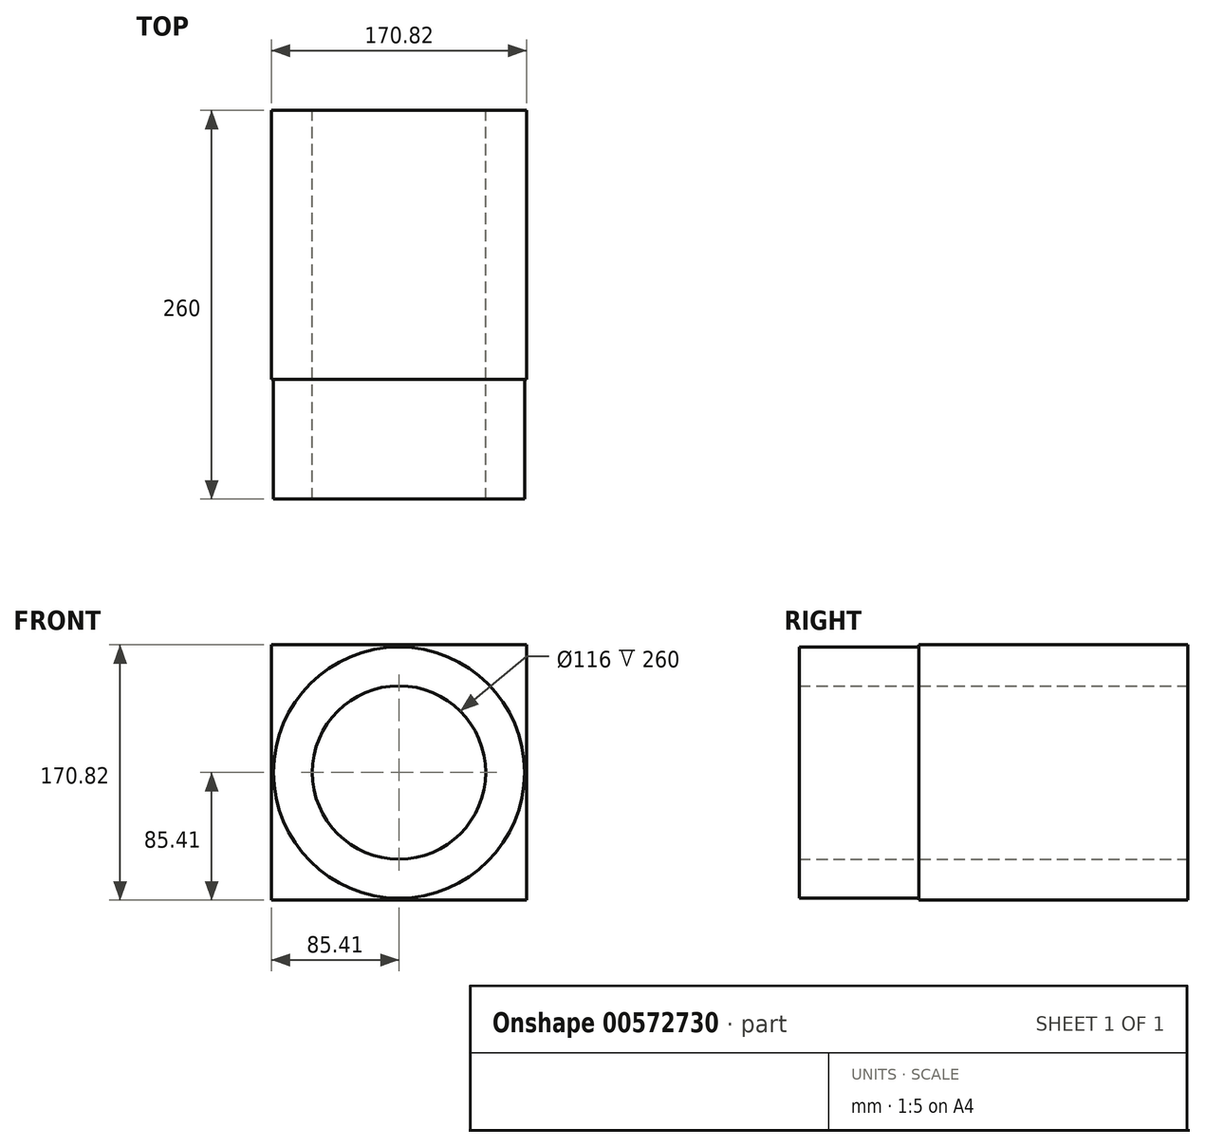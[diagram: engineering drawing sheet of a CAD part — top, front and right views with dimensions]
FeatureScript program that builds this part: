
annotation { "Feature Type Name" : "Feature", "Feature Type Description" : "" }
export const myFeature = defineFeature(function(context is Context, id is Id, definition is map)
    precondition{}
    {
        {
            var Q0;
            Q0=qCreatedBy(makeId("Front.planeOp"),FACE);
            var sketch = newSketch(context, id + "F0", { "sketchPlane" : qUnion([Q0])});
            skLineSegment(sketch, "E0.bottom", {"start": v(-85.4, 85.4) * mm, "end": v(85.4, 85.4) * mm});
            skLineSegment(sketch, "E0.top", {"start": v(-85.4, -85.4) * mm, "end": v(85.4, -85.4) * mm});
            skLineSegment(sketch, "E0.left", {"start": v(-85.4, 85.4) * mm, "end": v(-85.4, -85.4) * mm});
            skLineSegment(sketch, "E0.right", {"start": v(85.4, 85.4) * mm, "end": v(85.4, -85.4) * mm});
            skPoint(sketch, "E0.middle", {"position": v(0, 0) * mm});
            skCircle(sketch, "E1", {"center": v(0, 0) * mm, "radius": 58 * mm});
            skSolve(sketch);
        }
        {
            var Q0;
            Q0 = qSketchRegion(id + "F0", true);
            extrude(context, id + "F1", {"entities" : qUnion([Q0]), "depth" : 180 * mm, "offsetDistance" : 25 * mm});
        }
        {
            var Q0;
            Q0=makeQuery(id+"F1.opExtrude","CAP_FACE",FACE,{"disambiguationData":[OSD([sQuery(id+"F0.wireOp",EDGE,"E0.bottom"),sQuery(id+"F0.wireOp",EDGE,"E0.top"),sQuery(id+"F0.wireOp",EDGE,"E0.left"),sQuery(id+"F0.wireOp",EDGE,"E0.right"),sQuery(id+"F0.wireOp",EDGE,"E1")])],"isStart":false});
            var sketch = newSketch(context, id + "F2", { "sketchPlane" : qUnion([Q0])});
            skCircle(sketch, "E2.0", {"center": v(0, 0) * mm, "radius": 58 * mm});
            skCircle(sketch, "E3.0", {"center": v(0, 0) * mm, "radius": 84 * mm});
            skSolve(sketch);
        }
        {
            var Q0;
            Q0 = qSketchRegion(id + "F2", true);
            extrude(context, id + "F3", {"entities" : qUnion([Q0]), "operationType" : NewBodyOperationType.ADD, "depth" : 80 * mm, "offsetDistance" : 25 * mm});
        }
    });
